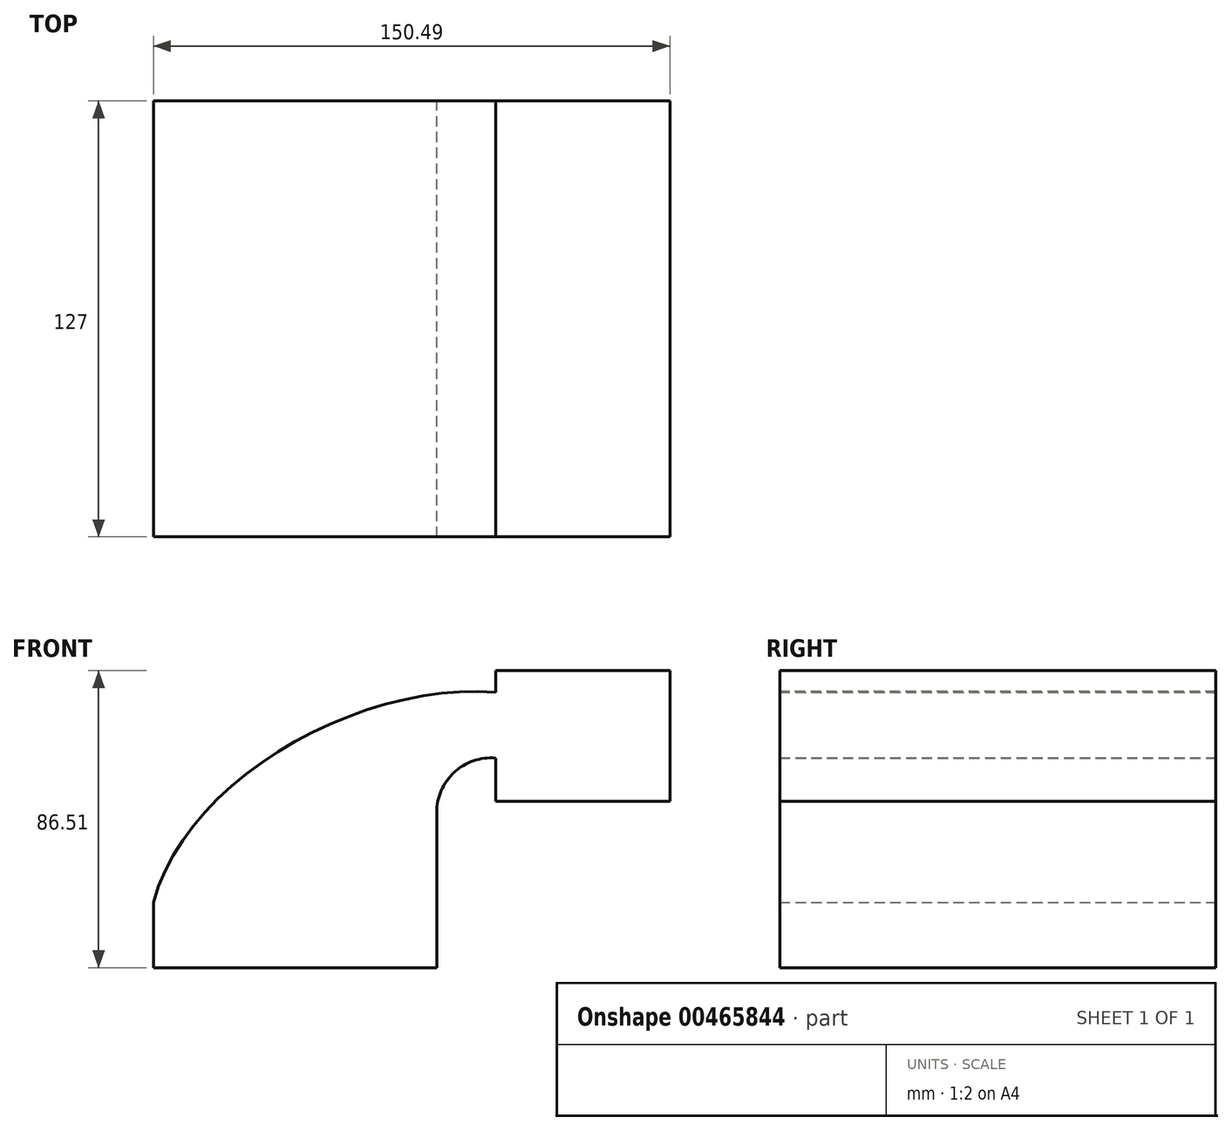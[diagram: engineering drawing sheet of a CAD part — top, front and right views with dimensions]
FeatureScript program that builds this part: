
annotation { "Feature Type Name" : "Feature", "Feature Type Description" : "" }
export const myFeature = defineFeature(function(context is Context, id is Id, definition is map)
    precondition{}
    {
        {
            var Q0;
            Q0=qCreatedBy(makeId("Front.planeOp"),FACE);
            var sketch = newSketch(context, id + "F0", { "sketchPlane" : qUnion([Q0])});
            skLineSegment(sketch, "E0.bottom", {"start": v(0, 0) * mm, "end": v(-82.55, 0) * mm});
            skLineSegment(sketch, "E0.top", {"start": v(0, -19.05) * mm, "end": v(-82.55, -19.05) * mm});
            skLineSegment(sketch, "E0.left", {"start": v(0, 0) * mm, "end": v(0, -19.05) * mm});
            skLineSegment(sketch, "E0.right", {"start": v(-82.55, 0) * mm, "end": v(-82.55, -19.05) * mm});
            skLineSegment(sketch, "E1.bottom", {"start": v(67.94, 67.46) * mm, "end": v(17.14, 67.46) * mm});
            skLineSegment(sketch, "E1.top", {"start": v(67.94, 29.36) * mm, "end": v(17.14, 29.36) * mm});
            skLineSegment(sketch, "E1.left", {"start": v(67.94, 67.46) * mm, "end": v(67.94, 29.36) * mm});
            skLineSegment(sketch, "E1.right", {"start": v(17.14, 67.46) * mm, "end": v(17.14, 29.36) * mm});
            skLineSegment(sketch, "E2", {"start": v(0, 0) * mm, "end": v(0, 26.21) * mm});
            skArc(sketch, "E3", {"start": v(0, 26.21) * mm, "mid": v(5.1, 37.88) * mm, "end": v(17.14, 42.04) * mm});
            skLineSegment(sketch, "E4", {"start": v(17.14, 42.04) * mm, "end": v(42.54, 42.04) * mm});
            skLineSegment(sketch, "E5.0", {"start": v(17.75, 61.09) * mm, "end": v(43.63, 61.09) * mm});
            skArc(sketch, "E5.1", {"start": v(-19.05, 26.21) * mm, "mid": v(-8.15, 51.56) * mm, "end": v(17.75, 61.09) * mm});
            skLineSegment(sketch, "E5.2", {"start": v(-19.05, 0) * mm, "end": v(-19.05, 26.21) * mm});
            skLineSegment(sketch, "E6", {"start": v(43.63, 61.09) * mm, "end": v(43.63, 29.36) * mm});
            skFitSpline(sketch, "E7", {"points": [v(-82.55, 0) * mm, v(17.75, 61.09) * mm], "startDerivative": vector(29.03, 109.1) * mm, "endDerivative": vector(117.8, -10.85) * mm});
            skSolve(sketch);
        }
        {
            var Q0;
            Q0 = qSketchRegion(id + "F0", true);
            extrude(context, id + "F1", {"entities" : qUnion([Q0]), "endBound" : BoundingType.SYMMETRIC, "depth" : 127 * mm});
        }
    });
